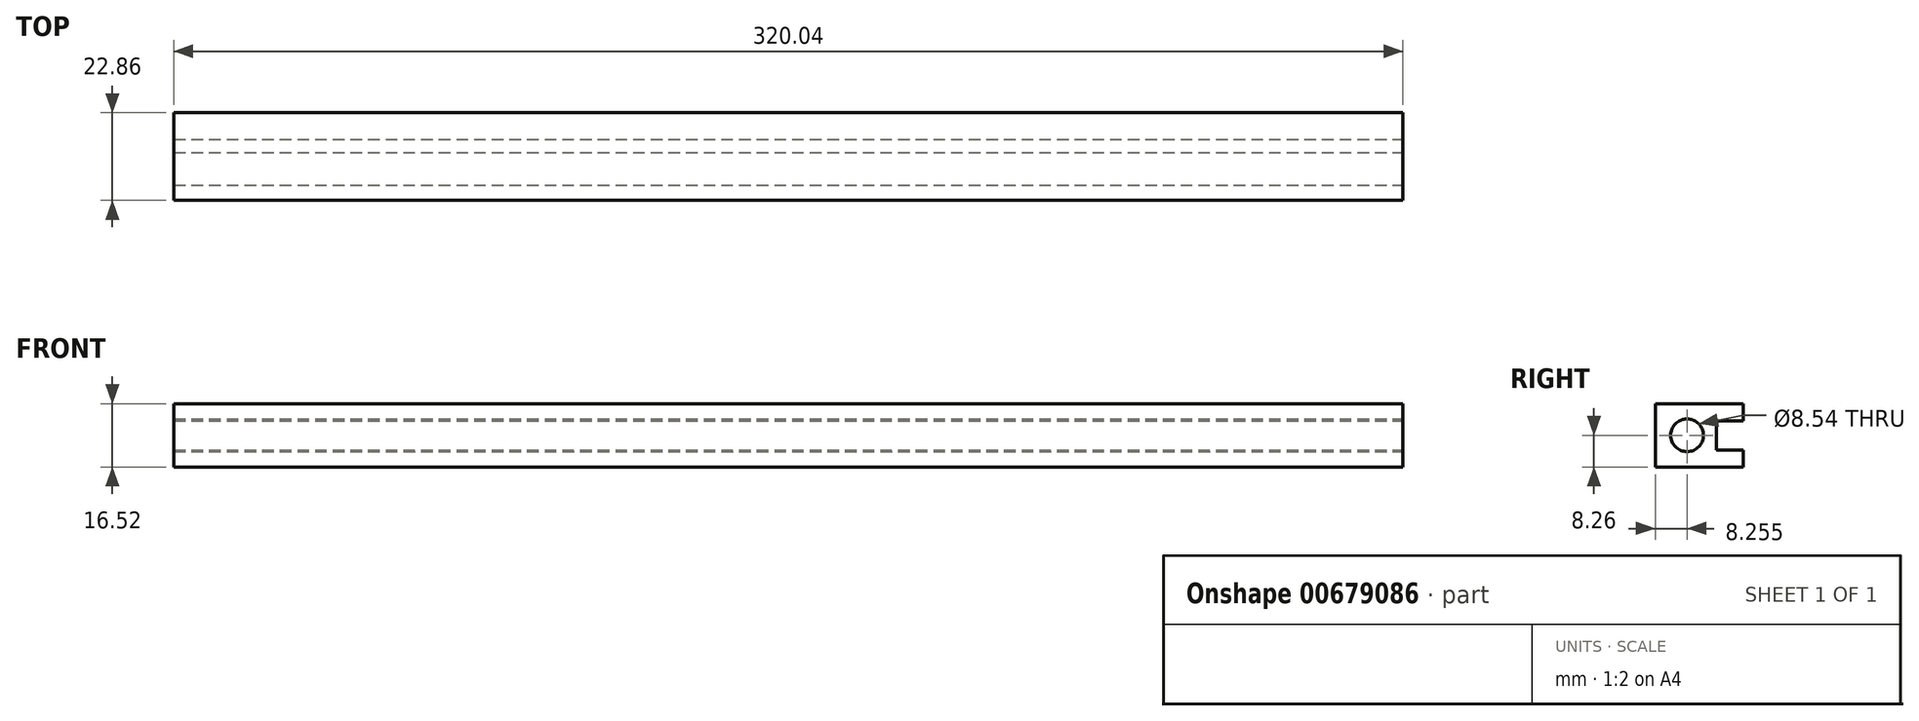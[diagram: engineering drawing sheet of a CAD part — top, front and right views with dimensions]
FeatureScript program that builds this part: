
annotation { "Feature Type Name" : "Feature", "Feature Type Description" : "" }
export const myFeature = defineFeature(function(context is Context, id is Id, definition is map)
    precondition{}
    {
        {
            var Q0;
            Q0=qCreatedBy(makeId("Front.planeOp"),FACE);
            var sketch = newSketch(context, id + "F0", { "sketchPlane" : qUnion([Q0])});
            skLineSegment(sketch, "E0.bottom", {"start": v(-160.02, 8.26) * mm, "end": v(160.02, 8.26) * mm});
            skLineSegment(sketch, "E0.top", {"start": v(-160.02, -8.26) * mm, "end": v(160.02, -8.26) * mm});
            skLineSegment(sketch, "E0.left", {"start": v(-160.02, 8.26) * mm, "end": v(-160.02, -8.26) * mm});
            skLineSegment(sketch, "E0.right", {"start": v(160.02, 8.26) * mm, "end": v(160.02, -8.26) * mm});
            skPoint(sketch, "E0.middle", {"position": v(0, 0) * mm});
            skLineSegment(sketch, "E1.left", {"start": v(-160.02, 3.81) * mm, "end": v(-160.02, -3.81) * mm});
            skLineSegment(sketch, "E1.right", {"start": v(160.02, 3.81) * mm, "end": v(160.02, -3.81) * mm});
            skSolve(sketch);
        }
        {
            var Q0;
            {var subQ3=sQuery(id+"F0.wireOp",EDGE,"E0.bottom");Q0=makeQuery(id+"F0.imprint","IMPRINT",FACE,{"disambiguationData":[TD([[makeQuery(id+"F0.imprint","IMPRINT",EDGE,{"derivedFrom":subQ3}),-1.0]])]});}
            extrude(context, id + "F1", {"entities" : qUnion([Q0]), "depth" : 22.86 * mm, "offsetDistance" : 25.4 * mm});
        }
        {
            var Q0;
            Q0=qCreatedBy(makeId("Front.planeOp"),FACE);
            var sketch = newSketch(context, id + "F2", { "sketchPlane" : qUnion([Q0])});
            skLineSegment(sketch, "E2.bottom", {"start": v(-160.02, 3.81) * mm, "end": v(160.02, 3.81) * mm});
            skLineSegment(sketch, "E2.top", {"start": v(-160.02, -3.81) * mm, "end": v(160.02, -3.81) * mm});
            skLineSegment(sketch, "E2.left", {"start": v(-160.02, 3.81) * mm, "end": v(-160.02, -3.81) * mm});
            skLineSegment(sketch, "E2.right", {"start": v(160.02, 3.81) * mm, "end": v(160.02, -3.81) * mm});
            skPoint(sketch, "E2.middle", {"position": v(0, 0) * mm});
            skSolve(sketch);
        }
        {
            var Q0;
            Q0 = qSketchRegion(id + "F2", true);
            extrude(context, id + "F3", {"entities" : qUnion([Q0]), "operationType" : NewBodyOperationType.REMOVE, "depth" : 7 * mm, "offsetDistance" : 25.4 * mm});
        }
        {
            var Q0;
            Q0=qCreatedBy(makeId("Right.planeOp"),FACE);
            var sketch = newSketch(context, id + "F4", { "sketchPlane" : qUnion([Q0])});
            skCircle(sketch, "E3", {"center": v(-14.6, 0) * mm, "radius": 4.27 * mm});
            skSolve(sketch);
        }
        {
            var Q0;
            Q0 = qSketchRegion(id + "F4", true);
            extrude(context, id + "F5", {"entities" : qUnion([Q0]), "operationType" : NewBodyOperationType.REMOVE, "endBound" : BoundingType.SYMMETRIC, "oppositeDirection" : true, "depth" : 320.04 * mm, "offsetDistance" : 25.4 * mm});
        }
    });
